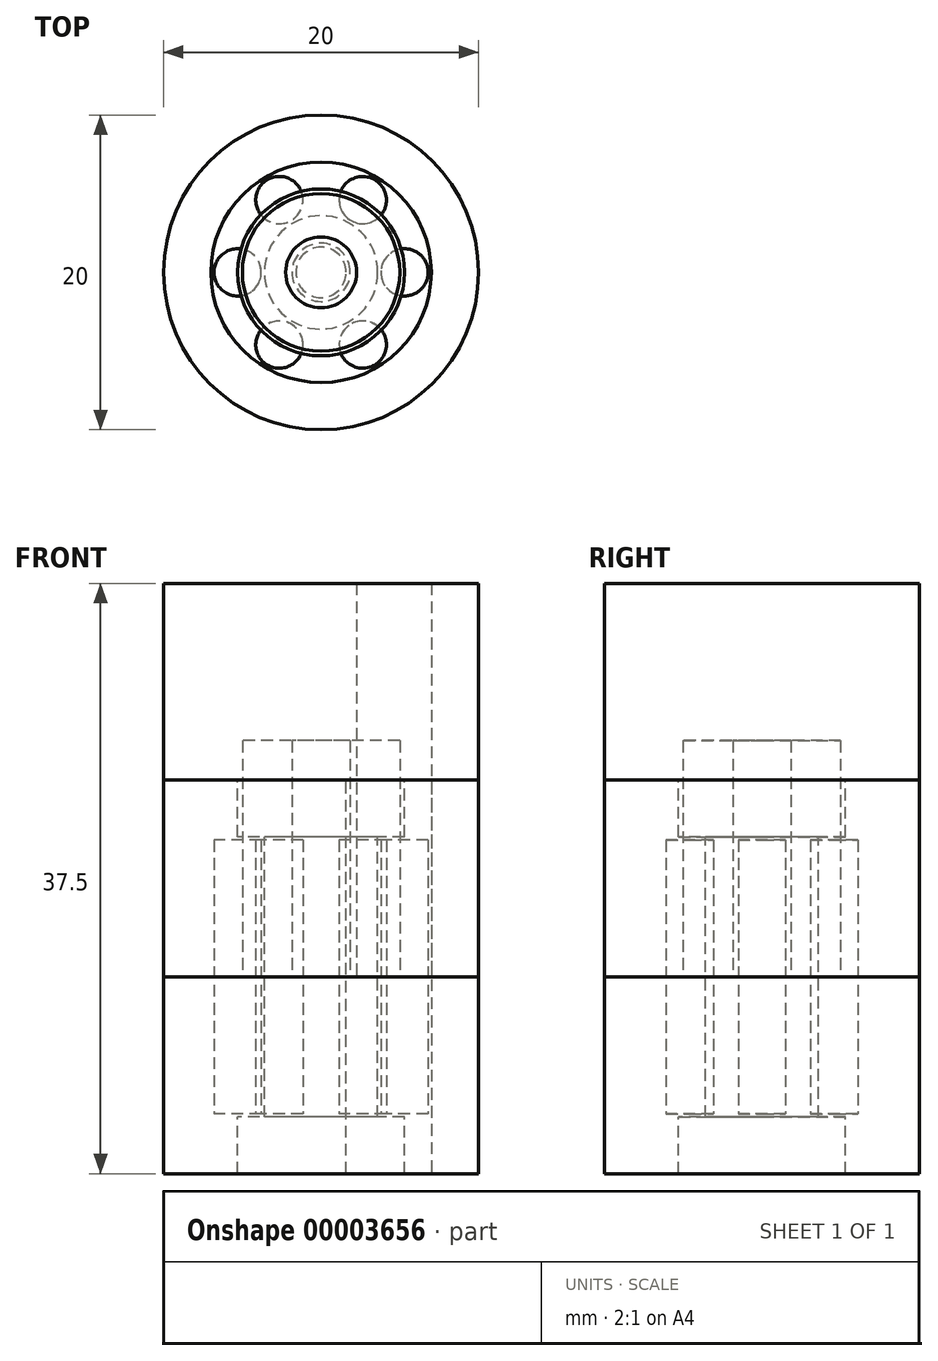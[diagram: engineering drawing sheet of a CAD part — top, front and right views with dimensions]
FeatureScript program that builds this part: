
annotation { "Feature Type Name" : "Feature", "Feature Type Description" : "" }
export const myFeature = defineFeature(function(context is Context, id is Id, definition is map)
    precondition{}
    {
        {
            var Q0;
            Q0=qCreatedBy(makeId("Top.planeOp"),FACE);
            var sketch = newSketch(context, id + "F0", { "sketchPlane" : qUnion([Q0])});
            skCircle(sketch, "E0", {"center": v(0, 0) * mm, "radius": 5 * mm});
            skCircle(sketch, "E1", {"center": v(0, 0) * mm, "radius": 1.85 * mm});
            skSolve(sketch);
        }
        {
            var Q0;
            Q0=makeQuery(id+"F0.imprint","IMPRINT",FACE,{"disambiguationData":[TD([[makeQuery(id+"F0.imprint","IMPRINT",EDGE,{"derivedFrom":sQuery(id+"F0.wireOp",EDGE,"E0")}),1.0]])]});
            extrude(context, id + "F1", {"entities" : qUnion([Q0]), "depth" : 15 * mm});
        }
        {
            var Q0;
            Q0=qCreatedBy(makeId("Top.planeOp"),FACE);
            var sketch = newSketch(context, id + "F2", { "sketchPlane" : qUnion([Q0])});
            skCircle(sketch, "E2", {"center": v(0, 0) * mm, "radius": 2.25 * mm});
            skSolve(sketch);
        }
        {
            var Q0;
            Q0=makeQuery(id+"F2.imprint","IMPRINT",FACE,{"disambiguationData":[TD([[makeQuery(id+"F2.imprint","IMPRINT",EDGE,{"derivedFrom":sQuery(id+"F2.wireOp",EDGE,"E2")}),1.0]])]});
            extrude(context, id + "F3", {"entities" : qUnion([Q0]), "depth" : 25 * mm});
        }
        {
            var Q0;
            Q0=qCreatedBy(makeId("Top.planeOp"),FACE);
            var sketch = newSketch(context, id + "F4", { "sketchPlane" : qUnion([Q0])});
            skPoint(sketch, "E3.rect.middle", {"position": v(0, 0) * mm});
            skCircle(sketch, "E4", {"center": v(0, 0) * mm, "radius": 7 * mm});
            skCircle(sketch, "E5", {"center": v(0, 0) * mm, "radius": 10 * mm});
            skSolve(sketch);
        }
        {
            var Q0;
            Q0=makeQuery(id+"F4.imprint","IMPRINT",FACE,{"disambiguationData":[TD([[makeQuery(id+"F4.imprint","IMPRINT",EDGE,{"derivedFrom":sQuery(id+"F4.wireOp",EDGE,"E4")}),-1.0]])]});
            extrude(context, id + "F5", {"entities" : qUnion([Q0]), "depth" : 25 * mm});
        }
        {
            var Q0;
            Q0=qCreatedBy(makeId("Top.planeOp"),FACE);
            var sketch = newSketch(context, id + "F6", { "sketchPlane" : qUnion([Q0])});
            skCircle(sketch, "E6.0", {"center": v(0, 0) * mm, "radius": 7 * mm});
            skCircle(sketch, "E7", {"center": v(0, 0) * mm, "radius": 5.3 * mm, "construction": true});
            skCircle(sketch, "E8", {"center": v(-5.3, 0) * mm, "radius": 1.5 * mm});
            skCircle(sketch, "E9", {"center": v(0, 0) * mm, "radius": 1.6 * mm});
            skCircle(sketch, "E10.1.0", {"center": v(-2.65, -4.59) * mm, "radius": 1.5 * mm});
            skCircle(sketch, "E10.2.0", {"center": v(2.65, -4.59) * mm, "radius": 1.5 * mm});
            skCircle(sketch, "E10.3.0", {"center": v(5.3, 0) * mm, "radius": 1.5 * mm});
            skCircle(sketch, "E10.4.0", {"center": v(2.65, 4.59) * mm, "radius": 1.5 * mm});
            skCircle(sketch, "E10.5.0", {"center": v(-2.65, 4.59) * mm, "radius": 1.5 * mm});
            skCircle(sketch, "E11", {"center": v(0, 0) * mm, "radius": 10 * mm});
            skSolve(sketch);
        }
        {
            var Q0;
            Q0=makeQuery(id+"F6.imprint","IMPRINT",FACE,{"disambiguationData":[TD([[makeQuery(id+"F6.imprint","IMPRINT",EDGE,{"derivedFrom":sQuery(id+"F6.wireOp",EDGE,"E6.0")}),-1.0]])]});
            extrude(context, id + "F7", {"entities" : qUnion([Q0]), "endBound" : BoundingType.SYMMETRIC, "depth" : 25 * mm});
        }
        {
            var Q0;
            Q0=makeQuery(id+"F6.imprint","IMPRINT",FACE,{"disambiguationData":[TD([[makeQuery(id+"F6.imprint","IMPRINT",EDGE,{"derivedFrom":sQuery(id+"F6.wireOp",EDGE,"E8")}),1.0]])]});
            var Q1;
            Q1=makeQuery(id+"F6.imprint","IMPRINT",FACE,{"disambiguationData":[TD([[makeQuery(id+"F6.imprint","IMPRINT",EDGE,{"derivedFrom":sQuery(id+"F6.wireOp",EDGE,"E10.1.0")}),1.0]])]});
            var Q2;
            Q2=makeQuery(id+"F6.imprint","IMPRINT",FACE,{"disambiguationData":[TD([[makeQuery(id+"F6.imprint","IMPRINT",EDGE,{"derivedFrom":sQuery(id+"F6.wireOp",EDGE,"E10.2.0")}),1.0]])]});
            var Q3;
            Q3=makeQuery(id+"F6.imprint","IMPRINT",FACE,{"disambiguationData":[TD([[makeQuery(id+"F6.imprint","IMPRINT",EDGE,{"derivedFrom":sQuery(id+"F6.wireOp",EDGE,"E10.3.0")}),1.0]])]});
            var Q4;
            Q4=makeQuery(id+"F6.imprint","IMPRINT",FACE,{"disambiguationData":[TD([[makeQuery(id+"F6.imprint","IMPRINT",EDGE,{"derivedFrom":sQuery(id+"F6.wireOp",EDGE,"E10.4.0")}),1.0]])]});
            var Q5;
            Q5=makeQuery(id+"F6.imprint","IMPRINT",FACE,{"disambiguationData":[TD([[makeQuery(id+"F6.imprint","IMPRINT",EDGE,{"derivedFrom":sQuery(id+"F6.wireOp",EDGE,"E10.5.0")}),1.0]])]});
            extrude(context, id + "F8", {"entities" : qUnion([Q0, Q1, Q2, Q3, Q4, Q5]), "endBound" : BoundingType.SYMMETRIC, "depth" : (25 - ((4 + 4) - (.2 * 2))) * mm});
        }
        {
            var Q0;
            Q0=makeQuery(id+"F6.imprint","IMPRINT",FACE,{"disambiguationData":[TD([[makeQuery(id+"F6.imprint","IMPRINT",EDGE,{"derivedFrom":sQuery(id+"F6.wireOp",EDGE,"E9")}),1.0]])]});
            extrude(context, id + "F9", {"entities" : qUnion([Q0]), "endBound" : BoundingType.SYMMETRIC, "depth" : 30 * mm});
        }
        {
            var Q0;
            Q0=qCreatedBy(makeId("Front.planeOp"),FACE);
            var sketch = newSketch(context, id + "F10", { "sketchPlane" : qUnion([Q0])});
            skLineSegment(sketch, "E12", {"start": v(-10.63, 0) * mm, "end": v(11.5, 0) * mm, "construction": true});
            skLineSegment(sketch, "E13", {"start": v(0, 16.79) * mm, "end": v(0, -15.88) * mm, "construction": true});
            skLineSegment(sketch, "E14", {"start": v(1.6, 12.5) * mm, "end": v(5.3, 12.5) * mm});
            skLineSegment(sketch, "E15", {"start": v(5.3, 12.5) * mm, "end": v(5.3, 8.9) * mm});
            skLineSegment(sketch, "E16", {"start": v(5.3, 8.9) * mm, "end": v(3.6, 8.9) * mm});
            skLineSegment(sketch, "E17", {"start": v(3.6, 8.9) * mm, "end": v(3.6, 0) * mm});
            skLineSegment(sketch, "E18", {"start": v(1.6, 0) * mm, "end": v(1.6, 12.5) * mm});
            skLineSegment(sketch, "E19.0.MirrorCS", {"start": v(1.6, 12.5) * mm, "end": v(1.6, 12.5) * mm});
            skLineSegment(sketch, "E20.0.MirrorCS", {"start": v(1.6, -12.5) * mm, "end": v(5.3, -12.5) * mm});
            skLineSegment(sketch, "E21.0.MirrorCS", {"start": v(1.6, 0) * mm, "end": v(1.6, -12.5) * mm});
            skLineSegment(sketch, "E22.0.MirrorCS", {"start": v(3.6, -8.9) * mm, "end": v(3.6, 0) * mm});
            skLineSegment(sketch, "E23.0.MirrorCS", {"start": v(5.3, -8.9) * mm, "end": v(3.6, -8.9) * mm});
            skLineSegment(sketch, "E24.0.MirrorCS", {"start": v(5.3, -12.5) * mm, "end": v(5.3, -8.9) * mm});
            skLineSegment(sketch, "E25.0", {"start": v(3.8, 8.7) * mm, "end": v(6.8, 8.7) * mm});
            skPoint(sketch, "E26", {"position": v(5.3, 8.7) * mm});
            skSolve(sketch);
        }
        {
            var Q0;
            Q0=makeQuery(id+"F10.imprint","IMPRINT",FACE,{"disambiguationData":[TD([[makeQuery(id+"F10.imprint","IMPRINT",EDGE,{"derivedFrom":sQuery(id+"F10.wireOp",EDGE,"E14")}),-1.0]])]});
            var Q1;
            Q1=sQuery(id+"F10.wireOp",EDGE,"E13");
            revolve(context, id + "F11", {"entities" : qUnion([Q0]), "axis" : qUnion([Q1]), "revolveType" : RevolveType.FULL});
        }
        {
            var Q0;
            Q0=makeQuery(id+"F11.opRevolve","SWEPT_FACE",FACE,{"disambiguationData":[OSD([sQuery(id+"F10.wireOp",EDGE,"E14")])]});
            var sketch = newSketch(context, id + "F12", { "sketchPlane" : qUnion([Q0])});
            skPoint(sketch, "E27", {"position": v(-5.3, 0) * mm});
            skPoint(sketch, "E28.1.0", {"position": v(-2.65, -4.59) * mm});
            skPoint(sketch, "E28.2.0", {"position": v(2.65, -4.59) * mm});
            skPoint(sketch, "E28.3.0", {"position": v(5.3, 0) * mm});
            skPoint(sketch, "E28.4.0", {"position": v(2.65, 4.59) * mm});
            skPoint(sketch, "E28.5.0", {"position": v(-2.65, 4.59) * mm});
            skPoint(sketch, "E28.center", {"position": v(0, 0) * mm});
            skSolve(sketch);
        }
        {
            var Q0;
            Q0=makeQuery(id+"F9.opExtrude","SWEPT_BODY",BODY,{"disambiguationData":[OSD([sQuery(id+"F6.wireOp",EDGE,"E9")])]});
            deleteBodies(context, id + "F13", {"entities" : qUnion([Q0])});
        }
    });
